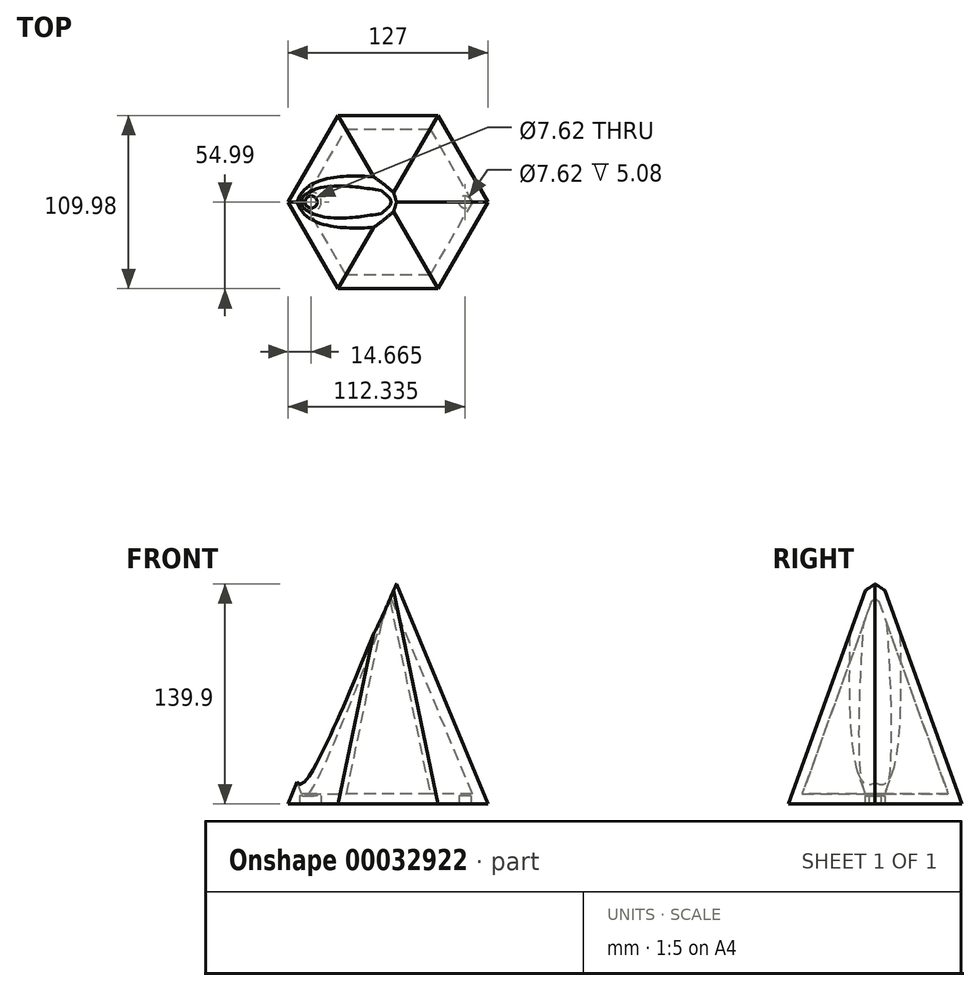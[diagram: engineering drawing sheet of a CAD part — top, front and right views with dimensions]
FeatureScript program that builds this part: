
annotation { "Feature Type Name" : "Feature", "Feature Type Description" : "" }
export const myFeature = defineFeature(function(context is Context, id is Id, definition is map)
    precondition{}
    {
        {
            var Q0;
            Q0=qCreatedBy(makeId("Top.planeOp"),FACE);
            var sketch = newSketch(context, id + "F0", { "sketchPlane" : qUnion([Q0])});
            skLineSegment(sketch, "E0", {"start": v(-63.5, 0) * mm, "end": v(-31.75, 55) * mm});
            skLineSegment(sketch, "E1", {"start": v(-31.75, 55) * mm, "end": v(31.75, 55) * mm});
            skLineSegment(sketch, "E2", {"start": v(31.75, 55) * mm, "end": v(63.5, 0) * mm});
            skLineSegment(sketch, "E3", {"start": v(63.5, 0) * mm, "end": v(31.75, -55) * mm});
            skLineSegment(sketch, "E4", {"start": v(31.75, -55) * mm, "end": v(-31.75, -55) * mm});
            skLineSegment(sketch, "E5", {"start": v(-31.75, -55) * mm, "end": v(-63.5, 0) * mm});
            skLineSegment(sketch, "E6", {"start": v(-63.5, 0) * mm, "end": v(63.5, 0) * mm, "construction": true});
            skLineSegment(sketch, "E7", {"start": v(31.75, 55) * mm, "end": v(-31.75, -55) * mm, "construction": true});
            skLineSegment(sketch, "E8", {"start": v(31.75, -55) * mm, "end": v(-31.75, 55) * mm, "construction": true});
            skLineSegment(sketch, "E9.0", {"start": v(-56.17, 0) * mm, "end": v(-28.08, 48.64) * mm});
            skLineSegment(sketch, "E9.1", {"start": v(-28.08, -48.64) * mm, "end": v(-56.17, 0) * mm});
            skLineSegment(sketch, "E9.2", {"start": v(28.08, -48.64) * mm, "end": v(-28.08, -48.64) * mm});
            skLineSegment(sketch, "E9.3", {"start": v(56.17, 0) * mm, "end": v(28.08, -48.64) * mm});
            skLineSegment(sketch, "E9.4", {"start": v(28.08, 48.64) * mm, "end": v(56.17, 0) * mm});
            skLineSegment(sketch, "E9.5", {"start": v(-28.08, 48.64) * mm, "end": v(28.08, 48.64) * mm});
            skArc(sketch, "E10", {"start": v(54.33, 3.18) * mm, "mid": v(42.49, 0) * mm, "end": v(54.33, -3.17) * mm});
            skCircle(sketch, "E11", {"center": v(48.84, 0) * mm, "radius": 3.81 * mm});
            skLineSegment(sketch, "E12", {"start": v(0, 9.25) * mm, "end": v(0, -9) * mm, "construction": true});
            skArc(sketch, "E13.MirrorCS", {"start": v(-54.33, 3.18) * mm, "mid": v(-42.49, 0) * mm, "end": v(-54.33, -3.17) * mm});
            skCircle(sketch, "E14.MirrorC", {"center": v(-48.84, 0) * mm, "radius": 3.81 * mm});
            skSolve(sketch);
        }
        {
            var Q0;
            Q0=makeQuery(id+"F0.imprint","IMPRINT",FACE,{"disambiguationData":[TD([[makeQuery(id+"F0.imprint","IMPRINT",EDGE,{"derivedFrom":sQuery(id+"F0.wireOp",EDGE,"E0")}),-1.0]])]});
            var Q1;
            {var subQ5=sQuery(id+"F0.wireOp",EDGE,"E9.2");Q1=makeQuery(id+"F0.imprint","IMPRINT",FACE,{"disambiguationData":[TD([[makeQuery(id+"F0.imprint","IMPRINT",EDGE,{"derivedFrom":subQ5}),-1.0]])]});}
            var Q2;
            {var subQ0=sQuery(id+"F0.wireOp",EDGE,"E10");Q2=makeQuery(id+"F0.imprint","IMPRINT",FACE,{"disambiguationData":[TD([[makeQuery(id+"F0.imprint","IMPRINT",EDGE,{"derivedFrom":subQ0}),1.0]])]});}
            var Q3;
            Q3=makeQuery(id+"F0.imprint","IMPRINT",FACE,{"disambiguationData":[TD([[makeQuery(id+"F0.imprint","IMPRINT",EDGE,{"derivedFrom":sQuery(id+"F0.wireOp",EDGE,"E11")}),1.0]])]});
            var Q4;
            Q4=makeQuery(id+"F0.imprint","IMPRINT",FACE,{"disambiguationData":[TD([[makeQuery(id+"F0.imprint","IMPRINT",EDGE,{"derivedFrom":sQuery(id+"F0.wireOp",EDGE,"E14.MirrorC")}),-1.0]])]});
            var Q5;
            {var subQ0=sQuery(id+"F0.wireOp",EDGE,"E13.MirrorCS");Q5=makeQuery(id+"F0.imprint","IMPRINT",FACE,{"disambiguationData":[TD([[makeQuery(id+"F0.imprint","IMPRINT",EDGE,{"derivedFrom":subQ0}),-1.0]])]});}
            extrude(context, id + "F1", {"entities" : qUnion([Q0, Q1, Q2, Q3, Q4, Q5]), "depth" : 152.4 * mm, "hasDraft" : true, "draftAngle" : 19.8 * degree, "draftPullDirection" : true});
        }
        {
            var Q0;
            {var subQ5=sQuery(id+"F0.wireOp",EDGE,"E9.2");Q0=makeQuery(id+"F0.imprint","IMPRINT",FACE,{"disambiguationData":[TD([[makeQuery(id+"F0.imprint","IMPRINT",EDGE,{"derivedFrom":subQ5}),-1.0]])]});}
            var Q1;
            {var subQ0=sQuery(id+"F0.wireOp",EDGE,"E10");Q1=makeQuery(id+"F0.imprint","IMPRINT",FACE,{"disambiguationData":[TD([[makeQuery(id+"F0.imprint","IMPRINT",EDGE,{"derivedFrom":subQ0}),1.0]])]});}
            var Q2;
            {var subQ0=sQuery(id+"F0.wireOp",EDGE,"E13.MirrorCS");Q2=makeQuery(id+"F0.imprint","IMPRINT",FACE,{"disambiguationData":[TD([[makeQuery(id+"F0.imprint","IMPRINT",EDGE,{"derivedFrom":subQ0}),-1.0]])]});}
            var Q3;
            Q3=makeQuery(id+"F0.imprint","IMPRINT",FACE,{"disambiguationData":[TD([[makeQuery(id+"F0.imprint","IMPRINT",EDGE,{"derivedFrom":sQuery(id+"F0.wireOp",EDGE,"E14.MirrorC")}),-1.0]])]});
            var Q4;
            Q4=makeQuery(id+"F0.imprint","IMPRINT",FACE,{"disambiguationData":[TD([[makeQuery(id+"F0.imprint","IMPRINT",EDGE,{"derivedFrom":sQuery(id+"F0.wireOp",EDGE,"E11")}),1.0]])]});
            extrude(context, id + "F2", {"entities" : qUnion([Q0, Q1, Q2, Q3, Q4]), "operationType" : NewBodyOperationType.REMOVE, "depth" : 152.4 * mm, "hasDraft" : true, "draftAngle" : 19.8 * degree, "draftPullDirection" : true});
        }
        {
            var Q0;
            {var subQ0=sQuery(id+"F0.wireOp",EDGE,"E10");Q0=makeQuery(id+"F0.imprint","IMPRINT",FACE,{"disambiguationData":[TD([[makeQuery(id+"F0.imprint","IMPRINT",EDGE,{"derivedFrom":subQ0}),1.0]])]});}
            var Q1;
            {var subQ0=sQuery(id+"F0.wireOp",EDGE,"E13.MirrorCS");Q1=makeQuery(id+"F0.imprint","IMPRINT",FACE,{"disambiguationData":[TD([[makeQuery(id+"F0.imprint","IMPRINT",EDGE,{"derivedFrom":subQ0}),-1.0]])]});}
            var Q2;
            Q2=makeQuery(id+"F0.imprint","IMPRINT",FACE,{"disambiguationData":[TD([[makeQuery(id+"F0.imprint","IMPRINT",EDGE,{"derivedFrom":sQuery(id+"F0.wireOp",EDGE,"E11")}),1.0]])]});
            var Q3;
            Q3=makeQuery(id+"F0.imprint","IMPRINT",FACE,{"disambiguationData":[TD([[makeQuery(id+"F0.imprint","IMPRINT",EDGE,{"derivedFrom":sQuery(id+"F0.wireOp",EDGE,"E14.MirrorC")}),-1.0]])]});
            extrude(context, id + "F3", {"entities" : qUnion([Q0, Q1, Q2, Q3]), "operationType" : NewBodyOperationType.ADD, "depth" : 6.35 * mm});
        }
        {
            var Q0;
            Q0=makeQuery(id+"F0.imprint","IMPRINT",FACE,{"disambiguationData":[TD([[makeQuery(id+"F0.imprint","IMPRINT",EDGE,{"derivedFrom":sQuery(id+"F0.wireOp",EDGE,"E11")}),1.0]])]});
            var Q1;
            Q1=makeQuery(id+"F0.imprint","IMPRINT",FACE,{"disambiguationData":[TD([[makeQuery(id+"F0.imprint","IMPRINT",EDGE,{"derivedFrom":sQuery(id+"F0.wireOp",EDGE,"E14.MirrorC")}),-1.0]])]});
            var Q2;
            Q2=sQuery(id+"F0.wireOp",EDGE,"E11");
            var Q3;
            Q3=sQuery(id+"F0.wireOp",EDGE,"E14.MirrorC");
            extrude(context, id + "F4", {"entities" : qUnion([Q0, Q1]), "operationType" : NewBodyOperationType.REMOVE, "surfaceEntities" : qUnion([Q2, Q3]), "depth" : 5.08 * mm});
        }
    });
